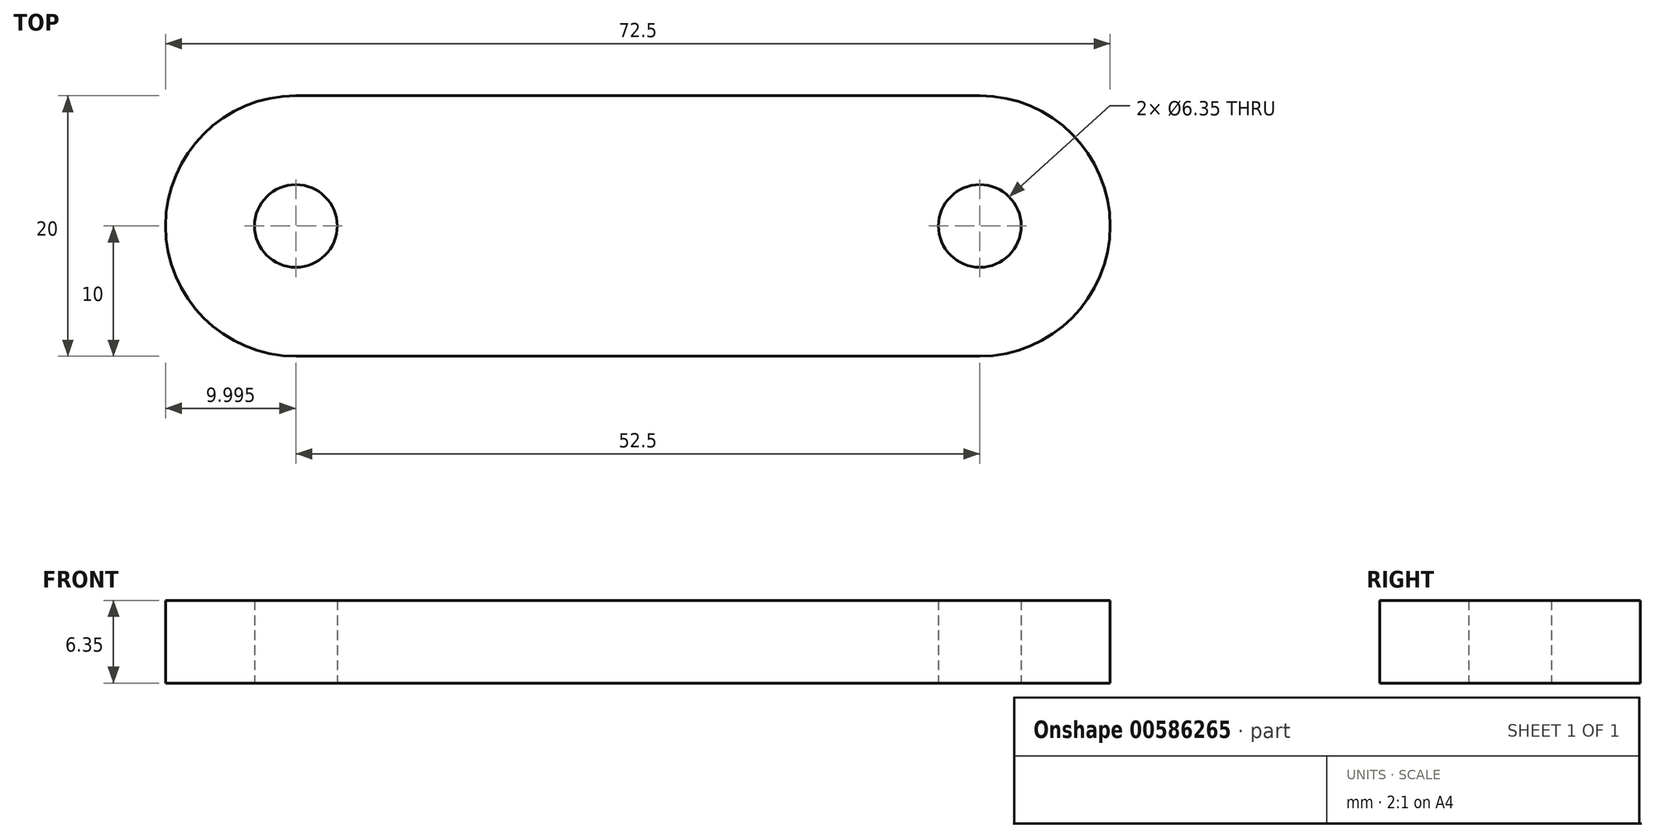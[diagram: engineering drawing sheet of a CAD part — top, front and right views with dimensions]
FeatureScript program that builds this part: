
annotation { "Feature Type Name" : "Feature", "Feature Type Description" : "" }
export const myFeature = defineFeature(function(context is Context, id is Id, definition is map)
    precondition{}
    {
        {
            var Q0;
            Q0=qCreatedBy(makeId("Top.planeOp"),FACE);
            var sketch = newSketch(context, id + "F0", { "sketchPlane" : qUnion([Q0])});
            skLineSegment(sketch, "E0", {"start": v(62.05, 0) * mm, "end": v(9.55, 0) * mm});
            skLineSegment(sketch, "E1", {"start": v(62.05, 20) * mm, "end": v(9.55, 20) * mm});
            skArc(sketch, "E2", {"start": v(62.05, 0) * mm, "mid": v(72.05, 10) * mm, "end": v(62.05, 20) * mm});
            skArc(sketch, "E3", {"start": v(9.55, 20) * mm, "mid": v(-0.45, 10) * mm, "end": v(9.55, 0) * mm});
            skSolve(sketch);
        }
        {
            var Q0;
            Q0=makeQuery(id+"F0.imprint","IMPRINT",FACE,{"disambiguationData":[TD([[makeQuery(id+"F0.imprint","IMPRINT",EDGE,{"derivedFrom":sQuery(id+"F0.wireOp",EDGE,"E0")}),-1.0]])]});
            var sketch = newSketch(context, id + "F1", { "sketchPlane" : qUnion([Q0])});
            skCircle(sketch, "E4", {"center": v(62.05, 10) * mm, "radius": 3.18 * mm});
            skCircle(sketch, "E5", {"center": v(9.55, 10) * mm, "radius": 3.18 * mm});
            skSolve(sketch);
        }
        {
            var Q0;
            Q0 = qSketchRegion(id + "F0", true);
            extrude(context, id + "F2", {"entities" : qUnion([Q0]), "depth" : 6.35 * mm, "offsetDistance" : 25 * mm});
        }
        {
            var Q0;
            Q0 = qSketchRegion(id + "F1", true);
            extrude(context, id + "F3", {"entities" : qUnion([Q0]), "operationType" : NewBodyOperationType.REMOVE, "endBound" : BoundingType.THROUGH_ALL, "depth" : 25 * mm, "offsetDistance" : 25 * mm});
        }
    });
